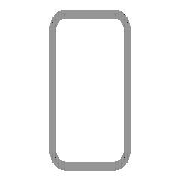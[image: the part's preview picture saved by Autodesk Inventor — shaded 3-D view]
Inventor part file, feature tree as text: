
AUTODESK INVENTOR PART (.ipt)
format: ipt  version: 2025 (Build 290162010, 162A)  size: 133,632 bytes
history: native  units: mm (DEFAULTED — no unit token found)
features: other x4, sketch x1, plane x1
ambient origin geometry x8: Origin, YZ Plane, XZ Plane, XY Plane, X Axis, Y Axis, Z Axis, Center Point
bodies: Solid1 (feature_tree), Body (feature_tree)
feature tree (6):
  parser-record x1  (decoder bookkeeping rows leaked as tree rows — omitted from the tree; the rows remain in map.json)
  other  "Driven Length"
  other  "Start Plane"
  other  "End Plane"
  sketch  "Sketch3"  dims[d3=3000.0mm d4=0.0mm d7=4.0mm d9=40.0mm d11=80.0mm d12=2.0mm d13=-0.0mm d14=3000.0mm d15=20.0mm d16=40.0mm d17=90.0deg d18=3000.0mm]
  plane  "Work Plane3"
